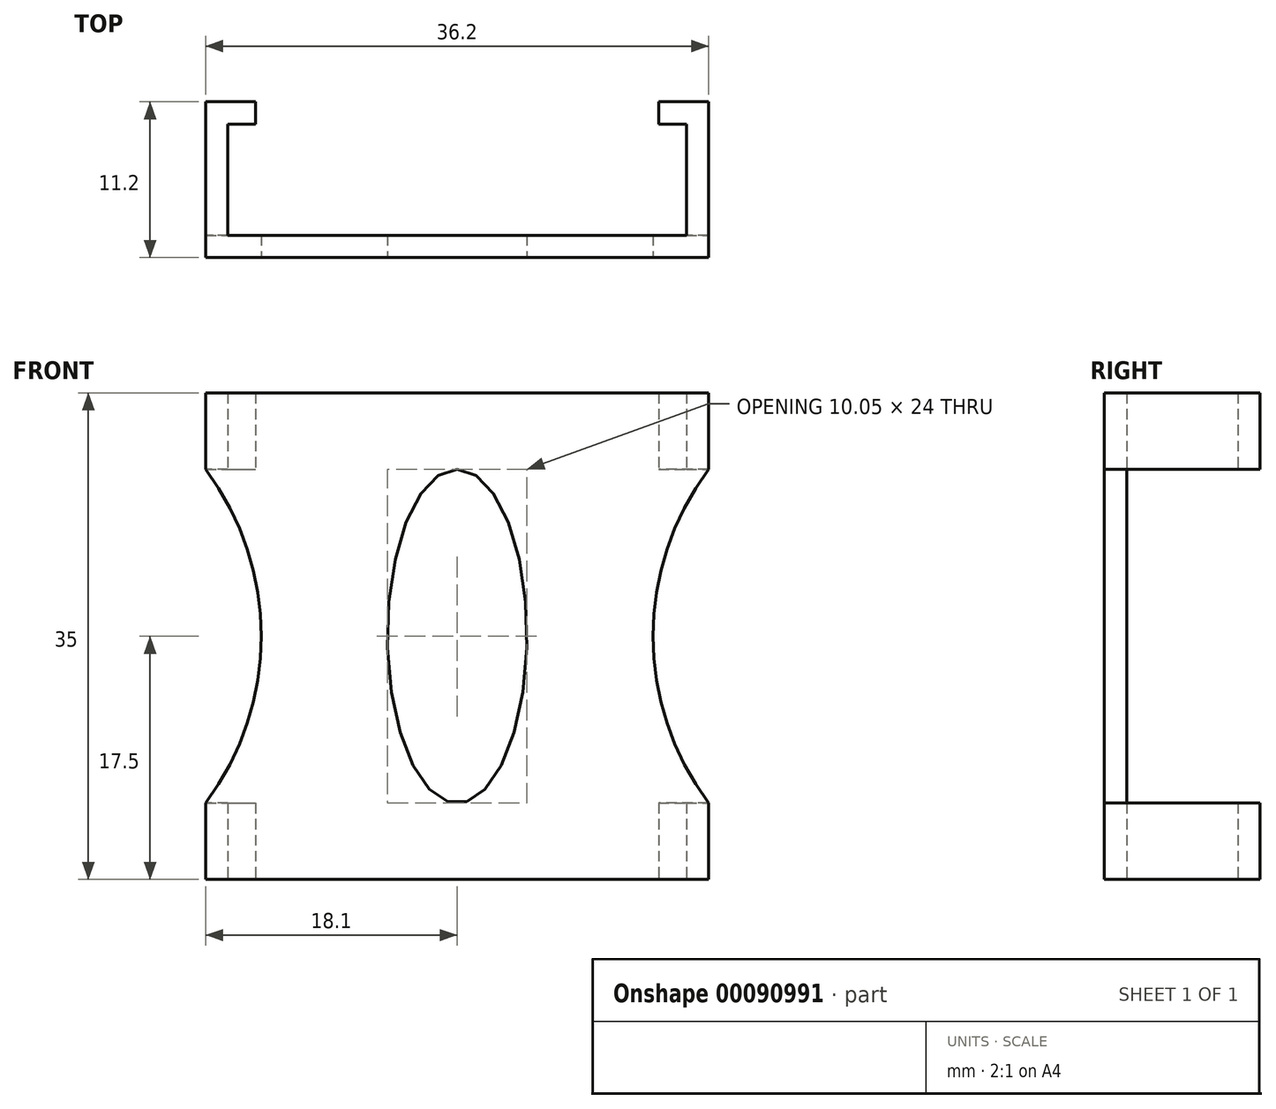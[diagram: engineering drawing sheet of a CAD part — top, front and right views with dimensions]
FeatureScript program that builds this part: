
annotation { "Feature Type Name" : "Feature", "Feature Type Description" : "" }
export const myFeature = defineFeature(function(context is Context, id is Id, definition is map)
    precondition{}
    {
        {
            var Q0;
            Q0=qCreatedBy(makeId("Top.planeOp"),FACE);
            var sketch = newSketch(context, id + "F0", { "sketchPlane" : qUnion([Q0])});
            skLineSegment(sketch, "E0", {"start": v(-16.5, 8) * mm, "end": v(-16.5, 0) * mm});
            skLineSegment(sketch, "E1", {"start": v(-16.5, 0) * mm, "end": v(16.5, 0) * mm});
            skLineSegment(sketch, "E2", {"start": v(16.5, 0) * mm, "end": v(16.5, 8) * mm});
            skLineSegment(sketch, "E3", {"start": v(16.5, 8) * mm, "end": v(14.5, 8) * mm});
            skLineSegment(sketch, "E4", {"start": v(-16.5, 8) * mm, "end": v(-14.5, 8) * mm});
            skLineSegment(sketch, "E5", {"start": v(0, 0.75) * mm, "end": v(0, 11.5) * mm, "construction": true});
            skLineSegment(sketch, "E6.0", {"start": v(18.1, 9.6) * mm, "end": v(14.5, 9.6) * mm});
            skLineSegment(sketch, "E6.1", {"start": v(-18.1, 9.6) * mm, "end": v(-14.5, 9.6) * mm});
            skLineSegment(sketch, "E6.2", {"start": v(-18.1, 9.6) * mm, "end": v(-18.1, -1.6) * mm});
            skLineSegment(sketch, "E6.3", {"start": v(-18.1, -1.6) * mm, "end": v(18.1, -1.6) * mm});
            skLineSegment(sketch, "E6.4", {"start": v(18.1, -1.6) * mm, "end": v(18.1, 9.6) * mm});
            skLineSegment(sketch, "E7", {"start": v(-14.5, 8) * mm, "end": v(-14.5, 9.6) * mm});
            skLineSegment(sketch, "E8", {"start": v(14.5, 8) * mm, "end": v(14.5, 9.6) * mm});
            skSolve(sketch);
        }
        {
            var Q0;
            Q0 = qSketchRegion(id + "F0", true);
            extrude(context, id + "F1", {"entities" : qUnion([Q0]), "endBound" : BoundingType.SYMMETRIC, "depth" : 35 * mm});
        }
        {
            var Q0;
            Q0=makeQuery(id+"F1.opExtrude","SWEPT_FACE",FACE,{"disambiguationData":[OSD([sQuery(id+"F0.wireOp",EDGE,"E6.3")])]});
            var sketch = newSketch(context, id + "F2", { "sketchPlane" : qUnion([Q0])});
            skArc(sketch, "E9", {"start": v(-18.1, -12) * mm, "mid": v(-14.1, 0) * mm, "end": v(-18.1, 12) * mm});
            skLineSegment(sketch, "E10", {"start": v(-18.1, 12) * mm, "end": v(-18.1, -12) * mm});
            skLineSegment(sketch, "E11", {"start": v(0, 0) * mm, "end": v(0, 11.25) * mm, "construction": true});
            skLineSegment(sketch, "E12.MirrorCS", {"start": v(18.1, 12) * mm, "end": v(18.1, -12) * mm});
            skArc(sketch, "E13.MirrorCS", {"start": v(18.1, -12) * mm, "mid": v(14.1, 0) * mm, "end": v(18.1, 12) * mm});
            skEllipse(sketch, "E14", {"center": v(0, 0) * mm, "majorRadius": 12 * mm, "minorRadius": 5.02 * mm, "majorAxis": v(0, 1)});
            skLineSegment(sketch, "E15", {"start": v(0, 12) * mm, "end": v(0, -12) * mm, "construction": true});
            skSolve(sketch);
        }
        {
            var Q0;
            Q0 = qSketchRegion(id + "F2", true);
            extrude(context, id + "F3", {"entities" : qUnion([Q0]), "operationType" : NewBodyOperationType.REMOVE, "oppositeDirection" : true, "depth" : 25 * mm});
        }
        {
            var Q0;
            {var subQ0=sQuery(id+"F0.wireOp",EDGE,"E7");var subQ1=sQuery(id+"F0.wireOp",EDGE,"E6.2");var subQ2=sQuery(id+"F0.wireOp",EDGE,"E6.1");Q0=makeQuery(id+"F3.boolean.opBoolean","SPLIT",FACE,{"disambiguationData":[TD([makeQuery(id+"F1.opExtrude","CAP_FACE",FACE,{"disambiguationData":[OSD([sQuery(id+"F0.wireOp",EDGE,"E0"),sQuery(id+"F0.wireOp",EDGE,"E1"),sQuery(id+"F0.wireOp",EDGE,"E2"),sQuery(id+"F0.wireOp",EDGE,"E3"),sQuery(id+"F0.wireOp",EDGE,"E4"),sQuery(id+"F0.wireOp",EDGE,"E6.0"),subQ2,subQ1,sQuery(id+"F0.wireOp",EDGE,"E6.3"),sQuery(id+"F0.wireOp",EDGE,"E6.4"),subQ0,sQuery(id+"F0.wireOp",EDGE,"E8")])],"isStart":false})])],"derivedFrom":makeQuery(id+"F1.opExtrude","SWEPT_FACE",FACE,{"disambiguationData":[OSD([subQ2])]})});}
            var sketch = newSketch(context, id + "F4", { "sketchPlane" : qUnion([Q0])});
            skLineSegment(sketch, "E16.bottom", {"start": v(-18.1, 12) * mm, "end": v(-14.5, 12) * mm});
            skLineSegment(sketch, "E16.top", {"start": v(-18.1, -12) * mm, "end": v(-14.5, -12) * mm});
            skLineSegment(sketch, "E16.left", {"start": v(-18.1, 12) * mm, "end": v(-18.1, -12) * mm});
            skLineSegment(sketch, "E16.right", {"start": v(-14.5, 12) * mm, "end": v(-14.5, -12) * mm});
            skLineSegment(sketch, "E17", {"start": v(0, 0) * mm, "end": v(0, 7.64) * mm, "construction": true});
            skLineSegment(sketch, "E18.MirrorCS", {"start": v(18.1, 12) * mm, "end": v(18.1, -12) * mm});
            skLineSegment(sketch, "E19.MirrorCS", {"start": v(18.1, 12) * mm, "end": v(14.5, 12) * mm});
            skLineSegment(sketch, "E20.MirrorCS", {"start": v(14.5, 12) * mm, "end": v(14.5, -12) * mm});
            skLineSegment(sketch, "E21.MirrorCS", {"start": v(18.1, -12) * mm, "end": v(14.5, -12) * mm});
            skSolve(sketch);
        }
        {
            var Q0;
            Q0 = qSketchRegion(id + "F4", true);
            var Q1;
            Q1=makeQuery(id+"F1.opExtrude","SWEPT_FACE",FACE,{"disambiguationData":[OSD([sQuery(id+"F0.wireOp",EDGE,"E1")])]});
            extrude(context, id + "F5", {"entities" : qUnion([Q0]), "operationType" : NewBodyOperationType.REMOVE, "endBound" : BoundingType.UP_TO_SURFACE, "oppositeDirection" : true, "endBoundEntityFace" : qUnion([Q1]), "depth" : 25 * mm});
        }
    });
